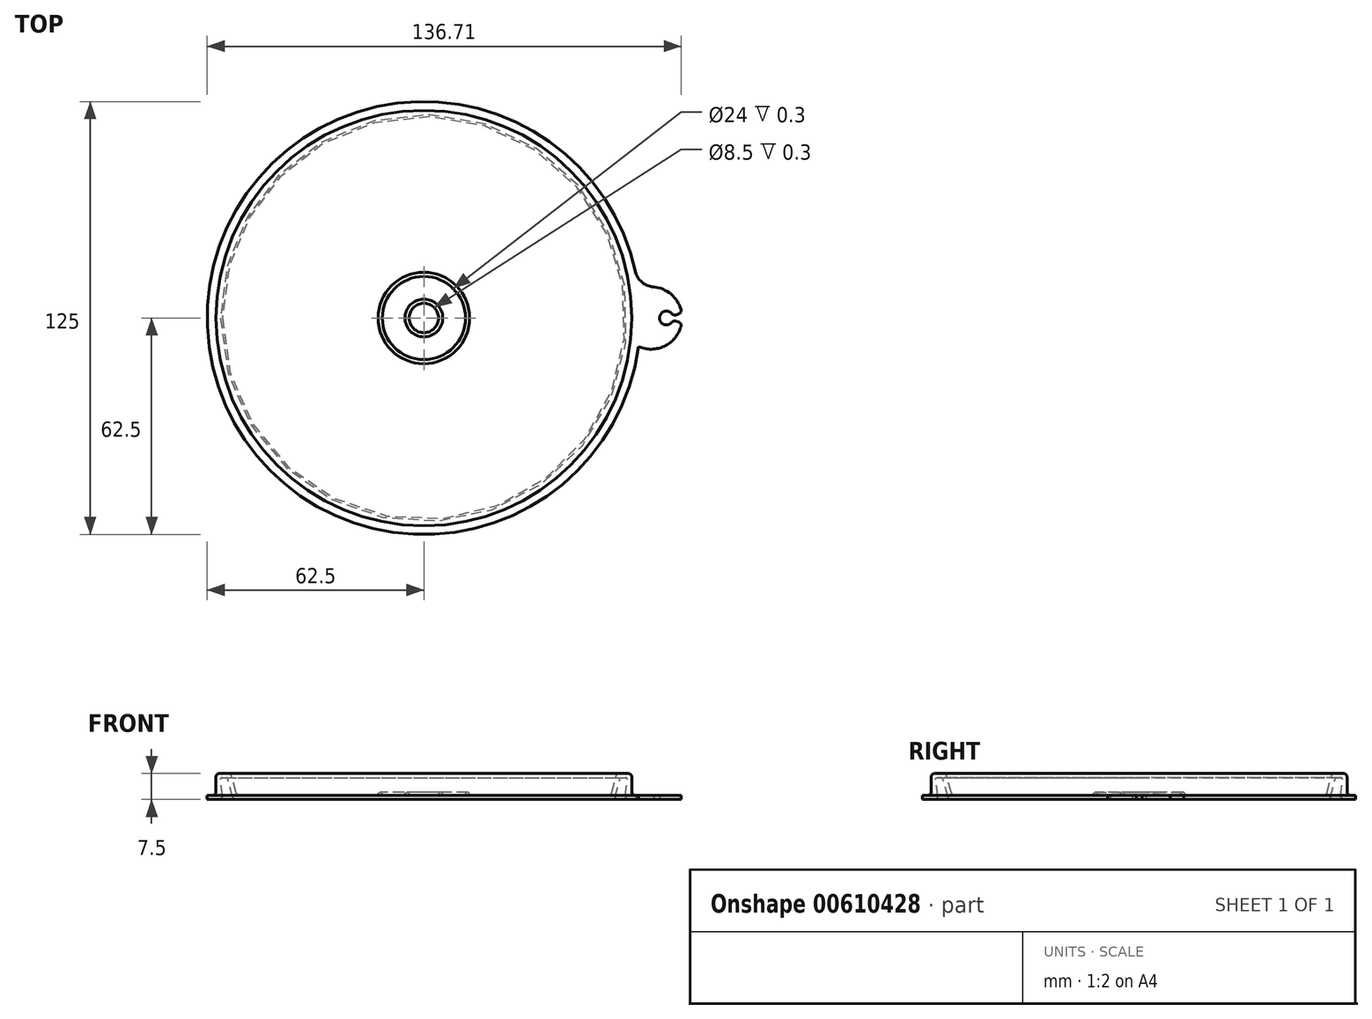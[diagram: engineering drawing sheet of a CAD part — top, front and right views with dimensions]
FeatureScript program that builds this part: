
annotation { "Feature Type Name" : "Feature", "Feature Type Description" : "" }
export const myFeature = defineFeature(function(context is Context, id is Id, definition is map)
    precondition{}
    {
        {
            var Q0;
            Q0=qCreatedBy(makeId("Top.planeOp"),FACE);
            var sketch = newSketch(context, id + "F0", { "sketchPlane" : qUnion([Q0])});
            skCircle(sketch, "E0", {"center": v(0, 0) * mm, "radius": 54 * mm});
            skPoint(sketch, "E1", {"position": v(54, 0) * mm});
            skCircle(sketch, "E2", {"center": v(0, 0) * mm, "radius": 59 * mm, "construction": true});
            skLineSegment(sketch, "E3", {"start": v(0, 0) * mm, "end": v(76.56, 0) * mm, "construction": true});
            skSolve(sketch);
        }
        {
            var Q0;
            Q0=qSketchRegion(id+"F0",true);
            extrude(context, id + "F1", {"entities" : qUnion([Q0]), "depth" : 1.2 * mm});
        }
        {
            var Q0;
            Q0=qCreatedBy(makeId("Front.planeOp"),FACE);
            var sketch = newSketch(context, id + "F2", { "sketchPlane" : qUnion([Q0])});
            skLineSegment(sketch, "E4", {"start": v(54, 0) * mm, "end": v(54.23, 0) * mm});
            skLineSegment(sketch, "E5", {"start": v(55.2, 0.74) * mm, "end": v(56.59, 5.93) * mm});
            skLineSegment(sketch, "E6", {"start": v(57.07, 6.3) * mm, "end": v(58.2, 6.3) * mm});
            skLineSegment(sketch, "E7", {"start": v(58.7, 5.74) * mm, "end": v(58.14, 1.12) * mm});
            skLineSegment(sketch, "E8", {"start": v(59.13, 0) * mm, "end": v(62.5, 0) * mm});
            skLineSegment(sketch, "E9", {"start": v(62.5, 0) * mm, "end": v(62.5, 1.2) * mm});
            skLineSegment(sketch, "E10", {"start": v(62.5, 1.2) * mm, "end": v(60.97, 1.2) * mm});
            skLineSegment(sketch, "E11", {"start": v(59.97, 2.2) * mm, "end": v(59.97, 6.5) * mm});
            skLineSegment(sketch, "E12", {"start": v(58.97, 7.5) * mm, "end": v(56.46, 7.5) * mm});
            skLineSegment(sketch, "E13", {"start": v(55.49, 6.76) * mm, "end": v(54, 1.2) * mm});
            skLineSegment(sketch, "E14", {"start": v(54, 1.2) * mm, "end": v(54, 0) * mm});
            skPoint(sketch, "E15.visualSharp", {"position": v(55.69, 7.5) * mm});
            skArc(sketch, "E15.filletArc", {"start": v(56.46, 7.5) * mm, "mid": v(55.85, 7.3) * mm, "end": v(55.49, 6.76) * mm});
            skPoint(sketch, "E16.visualSharp", {"position": v(59.97, 7.5) * mm});
            skArc(sketch, "E16.filletArc", {"start": v(59.97, 6.5) * mm, "mid": v(59.68, 7.2) * mm, "end": v(58.97, 7.5) * mm});
            skPoint(sketch, "E17.visualSharp", {"position": v(59.97, 1.2) * mm});
            skArc(sketch, "E17.filletArc", {"start": v(59.97, 2.2) * mm, "mid": v(60.27, 1.5) * mm, "end": v(60.97, 1.2) * mm});
            skPoint(sketch, "E18.visualSharp", {"position": v(55, 0) * mm});
            skArc(sketch, "E18.filletArc", {"start": v(54.23, 0) * mm, "mid": v(54.84, 0.2) * mm, "end": v(55.2, 0.74) * mm});
            skPoint(sketch, "E19.visualSharp", {"position": v(58, 0) * mm});
            skArc(sketch, "E19.filletArc", {"start": v(58.14, 1.12) * mm, "mid": v(58.38, 0.34) * mm, "end": v(59.13, 0) * mm});
            skPoint(sketch, "E20.visualSharp", {"position": v(56.69, 6.3) * mm});
            skArc(sketch, "E20.filletArc", {"start": v(57.07, 6.3) * mm, "mid": v(56.77, 6.2) * mm, "end": v(56.59, 5.93) * mm});
            skPoint(sketch, "E21.visualSharp", {"position": v(58.77, 6.3) * mm});
            skArc(sketch, "E21.filletArc", {"start": v(58.7, 5.74) * mm, "mid": v(58.58, 6.13) * mm, "end": v(58.2, 6.3) * mm});
            skLineSegment(sketch, "E22", {"start": v(0, -3.65) * mm, "end": v(0, 8.92) * mm, "construction": true});
            skSolve(sketch);
        }
        {
            var Q0;
            Q0=qSketchRegion(id+"F2",true);
            var Q1;
            Q1=sQuery(id+"F2.wireOp",EDGE,"E22");
            revolve(context, id + "F3", {"operationType" : NewBodyOperationType.ADD, "entities" : qUnion([Q0]), "axis" : qUnion([Q1]), "revolveType" : RevolveType.FULL});
        }
        {
            var Q0;
            Q0=makeQuery(id+"F1.opExtrude","CAP_FACE",FACE,{"disambiguationData":[OSD([sQuery(id+"F0.wireOp",EDGE,"E0")])],"isStart":false});
            fillet(context, id + "F4", {"entities" : qUnion([Q0]), "radius" : 1 * mm, "tangentPropagation" : true, "allowEdgeOverflow" : false});
        }
        {
            var Q0;
            Q0=qCreatedBy(makeId("Top.planeOp"),FACE);
            var sketch = newSketch(context, id + "F5", { "sketchPlane" : qUnion([Q0])});
            skCircle(sketch, "E23", {"center": v(70, 0) * mm, "radius": 2 * mm});
            skCircle(sketch, "E24", {"center": v(65.5, 0) * mm, "radius": 9 * mm});
            skCircle(sketch, "E25", {"center": v(0, 0) * mm, "radius": 62.5 * mm});
            skArc(sketch, "E26", {"start": v(61.15, 12.93) * mm, "mid": v(63.14, 10.17) * mm, "end": v(66.32, 8.96) * mm});
            skLineSegment(sketch, "E27", {"start": v(91.8, 0) * mm, "end": v(58.55, 0) * mm, "construction": true});
            skArc(sketch, "E28.MirrorCS", {"start": v(61.15, -12.93) * mm, "mid": v(63.14, -10.17) * mm, "end": v(66.32, -8.96) * mm});
            skLineSegment(sketch, "E29", {"start": v(70, 0) * mm, "end": v(75.18, 1.75) * mm});
            skLineSegment(sketch, "E30", {"start": v(75.18, 1.75) * mm, "end": v(75.18, -1.75) * mm});
            skLineSegment(sketch, "E31", {"start": v(75.18, -1.75) * mm, "end": v(70, 0) * mm});
            skPoint(sketch, "E32", {"position": v(75.18, 0) * mm});
            skSolve(sketch);
        }
        {
            var Q0;
            {var subQ4=sQuery(id+"F5.wireOp",EDGE,"E29");var subQ8=sQuery(id+"F5.wireOp",EDGE,"E23");var subQ9=makeQuery(id+"F5.imprint","INTERSECT",VERTEX,{"derivedFrom":[subQ8,subQ4]});Q0=makeQuery(id+"F5.imprint","IMPRINT",FACE,{"disambiguationData":[TD([[makeQuery(id+"F5.imprint","IMPRINT",EDGE,{"disambiguationData":[TD([[subQ9,-1.0]])],"derivedFrom":subQ8}),-1.0]])]});}
            var Q1;
            {var subQ0=sQuery(id+"F5.wireOp",EDGE,"E28.MirrorCS");Q1=makeQuery(id+"F5.imprint","IMPRINT",FACE,{"disambiguationData":[TD([[makeQuery(id+"F5.imprint","IMPRINT",EDGE,{"derivedFrom":subQ0}),1.0]])]});}
            var Q2;
            {var subQ0=sQuery(id+"F5.wireOp",EDGE,"E26");Q2=makeQuery(id+"F5.imprint","IMPRINT",FACE,{"disambiguationData":[TD([[makeQuery(id+"F5.imprint","IMPRINT",EDGE,{"derivedFrom":subQ0}),-1.0]])]});}
            extrude(context, id + "F6", {"entities" : qUnion([Q0, Q1, Q2]), "operationType" : NewBodyOperationType.ADD, "depth" : 1.2 * mm});
        }
        {
            var Q0;
            Q0=makeQuery(id+"F6.opExtrude","SWEPT_EDGE",EDGE,{"disambiguationData":[OSD([sQuery(id+"F5.wireOp",EDGE,"E24"),sQuery(id+"F5.wireOp",EDGE,"E29")])]});
            var Q1;
            Q1=makeQuery(id+"F6.opExtrude","SWEPT_EDGE",EDGE,{"disambiguationData":[OSD([sQuery(id+"F5.wireOp",EDGE,"E24"),sQuery(id+"F5.wireOp",EDGE,"E31")])]});
            var Q2;
            Q2=makeQuery(id+"F6.opExtrude","SWEPT_EDGE",EDGE,{"disambiguationData":[OSD([sQuery(id+"F5.wireOp",EDGE,"E23"),sQuery(id+"F5.wireOp",EDGE,"E29")])]});
            var Q3;
            Q3=makeQuery(id+"F6.opExtrude","SWEPT_EDGE",EDGE,{"disambiguationData":[OSD([sQuery(id+"F5.wireOp",EDGE,"E23"),sQuery(id+"F5.wireOp",EDGE,"E31")])]});
            fillet(context, id + "F7", {"entities" : qUnion([Q0, Q1, Q2, Q3]), "radius" : 1 * mm, "tangentPropagation" : true, "allowEdgeOverflow" : false});
        }
        {
            var Q0;
            Q0=makeQuery(id+"F1.opExtrude","CAP_FACE",FACE,{"disambiguationData":[OSD([sQuery(id+"F0.wireOp",EDGE,"E0")])],"isStart":false});
            var sketch = newSketch(context, id + "F8", { "sketchPlane" : qUnion([Q0])});
            skCircle(sketch, "E33", {"center": v(0, 0) * mm, "radius": 4.25 * mm});
            skCircle(sketch, "E34", {"center": v(0, 0) * mm, "radius": 5.45 * mm});
            skCircle(sketch, "E35", {"center": v(0, 0) * mm, "radius": 12 * mm});
            skCircle(sketch, "E36", {"center": v(0, 0) * mm, "radius": 13.2 * mm});
            skSolve(sketch);
        }
        {
            var Q0;
            Q0=makeQuery(id+"F8.imprint","IMPRINT",FACE,{"disambiguationData":[TD([[makeQuery(id+"F8.imprint","IMPRINT",EDGE,{"derivedFrom":sQuery(id+"F8.wireOp",EDGE,"E33")}),-1.0]])]});
            var Q1;
            Q1=makeQuery(id+"F8.imprint","IMPRINT",FACE,{"disambiguationData":[TD([[makeQuery(id+"F8.imprint","IMPRINT",EDGE,{"derivedFrom":sQuery(id+"F8.wireOp",EDGE,"E35")}),-1.0]])]});
            extrude(context, id + "F9", {"entities" : qUnion([Q0, Q1]), "operationType" : NewBodyOperationType.ADD, "depth" : 0.8 * mm});
        }
        {
            var Q0;
            Q0=makeQuery(id+"F9.opExtrude","CAP_EDGE",EDGE,{"disambiguationData":[OSD([sQuery(id+"F8.wireOp",EDGE,"E36")])],"isStart":false});
            var Q1;
            Q1=makeQuery(id+"F9.opExtrude","CAP_EDGE",EDGE,{"disambiguationData":[OSD([sQuery(id+"F8.wireOp",EDGE,"E34")])],"isStart":false});
            var Q2;
            Q2=makeQuery(id+"F9.opExtrude","CAP_EDGE",EDGE,{"disambiguationData":[OSD([sQuery(id+"F8.wireOp",EDGE,"E35")])],"isStart":false});
            var Q3;
            Q3=makeQuery(id+"F9.opExtrude","CAP_EDGE",EDGE,{"disambiguationData":[OSD([sQuery(id+"F8.wireOp",EDGE,"E33")])],"isStart":false});
            fillet(context, id + "F10", {"entities" : qUnion([Q0, Q1, Q2, Q3]), "radius" : .5 * mm, "tangentPropagation" : true, "allowEdgeOverflow" : false});
        }
    });
